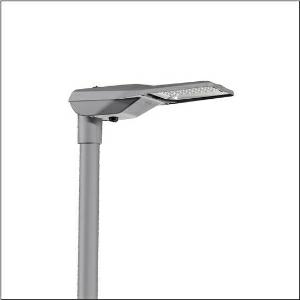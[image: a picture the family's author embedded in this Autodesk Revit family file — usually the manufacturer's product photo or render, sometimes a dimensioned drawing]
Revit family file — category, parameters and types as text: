
# Revit family: streetlight_sl_21_mini___p0_8a_5xe2u33t08gb_af06
name_source: partatom
category: Lighting Fixtures
units: mm (PartAtom-declared; Revit-internal decimal feet)

## family parameters
Cut with Voids When Loaded = No
Host = Face
Light Source = No
Part Type = Normal
Room Calculation Point = No
Round Connector Dimension = Use Diameter
Shared = No

## types (1)
- --- (1 x LED, 5990 lm, 40.4 W, 3000K)
    Apparent Load = 40 VA
    CIE Flux Codes = 33 69 96 100 100
    Color Rendering = 70
    Color Temperature = 3000K
    Default Elevation = 1800 mm
    Description = Streetlight SL 21 mini, mast luminaire, primary light control with lens, of PMMA, primary optical cover: cover, of toughened safety glass, transparent, light distribution: P0.8a, light emission: direct distribution, primary light characteristic: asymmetric, installation type: post-top, side-entry, LED, High Power LED, rated luminous flux: 5.990lm, luminous efficacy: 148lm/W, light colour: 730, colour temperature: 3000K, control gear: D4i, control: pre-setting: logarithmic dimming characteristic, flexible luminous flux parameterisation, time-dependent luminous flux control, constant luminous flux control, overheat protection, mains connection: 220..240V, AC, 50/60Hz, start of lifetime: 40W, end of service life: 41W, reduction: 19W, luminaire housing, of diecast aluminium, powder-coated, SITECO metallic grey (DB 702S), corrosivity category C5 high according to DIN EN ISO 12944, multi-level sealing system, sealing non-destructively replaceable, inclination adjustable: 0°, 5°, 10°, 15°, please order mast flange separately, length: 628mm, width: 235mm, height: 110mm, mast flange for spigot size: 42mm (side-entry): 5XC10008XM4, 60/48mm (side-entry/post-top): 5XC10108XM2, 76/60mm (side-entry/post-top): 5XC10108XM1, mounting height: 4..8m, Smart Interface below and above, protection rating (complete): IP66, insulation class (complete): insulation class II (safety insulation), certification: CE, ENEC, ENEC+, VDE, impact resistance: IK10, permissible operating ambient temperature for outdoor applications: -40..+50°C, standard-compliant lighting for roads and squares, packaging unit: 1 piece

Light Distribution: P0.8a
    Height = 110 mm
    Lamp = 1 x LED
    Lamp Light Flux = 5990 lm
    Lamp Power = 40.4 W
    Lamp count = 1
    Length = 625 mm
    Luminous efficacy = 148 lm/W
    Manufacturer = Siteco
    ModVariant = No
    Model = 5XE2U33T08GB
    Number of Poles = 1
    OnlyDefault = Yes
    Power Factor = 1
    Product Name = Streetlight SL 21 mini | P0.8a
    Product group = mast luminaire | pylon top
    ProductGroupID = 6100
    Protection Class = Protection class II
    Protection Degree = IP 66
    RLX_Detail_Level = 1
    RLX_Emergency_Light_Flux = 0 lm
    RLX_Emergency_Type = 0
    RLX_Emergency_Type_DB = No
    RlxData = <blob elided: 92773 chars, md5=c7edc812>
    Socket = socket
    Standby Power = 0 W
    System Light Flux = 5990 lm
    System Power = 40 W
    Type Comments = factory setting: luminous flux: 100 % | dim-lin: 254 | 812 mA
    Type Image = l_1003514.jpg
    URL = http://relux.com
    VarID = @adj_079953
    Voltage = 0 V
    Weight = 0.00 kg
    Width = 234 mm

## geometry (parser evidence)
native form markers: Blend x4, Sweep x11
no freeform markers — native parametric forms only
